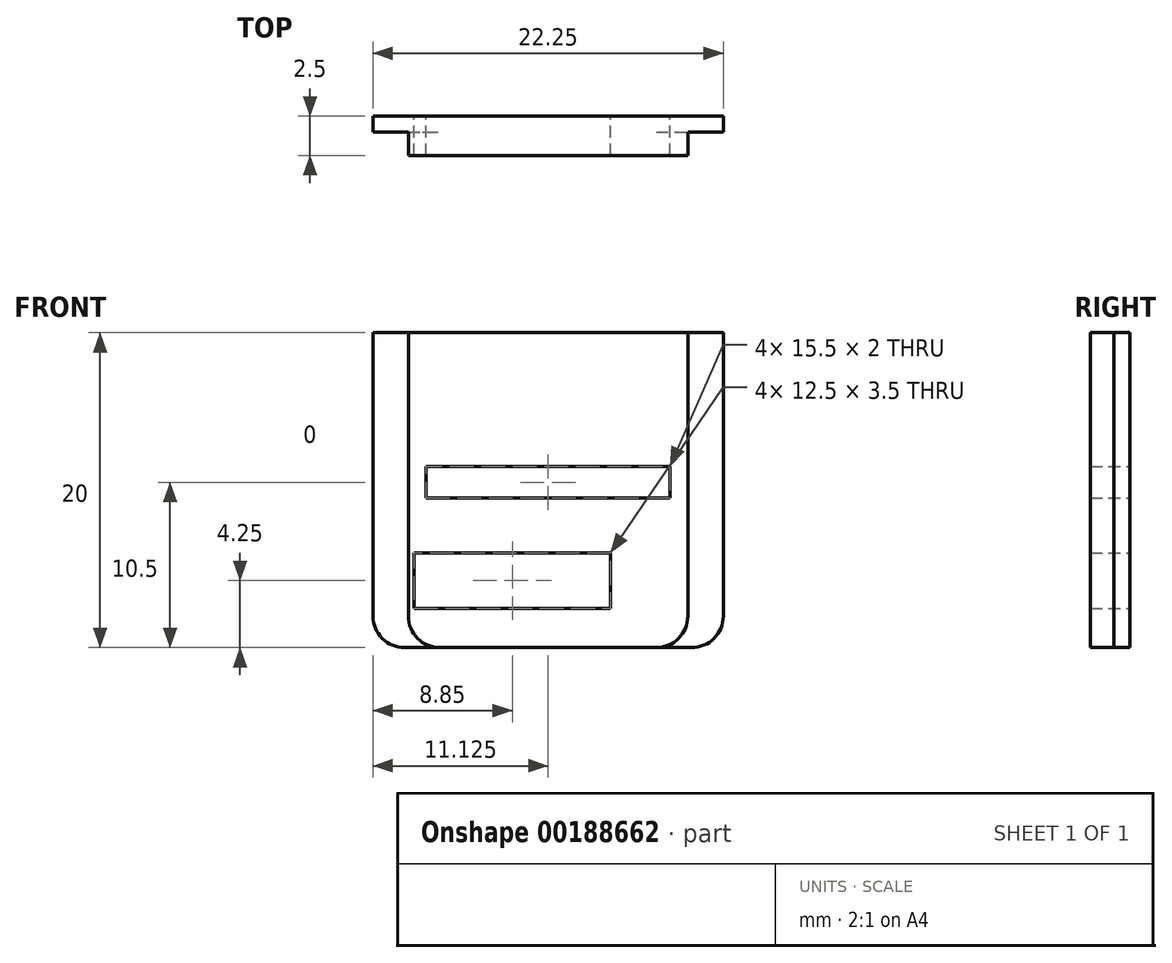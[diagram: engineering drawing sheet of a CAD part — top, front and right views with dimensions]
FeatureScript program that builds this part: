
annotation { "Feature Type Name" : "Feature", "Feature Type Description" : "" }
export const myFeature = defineFeature(function(context is Context, id is Id, definition is map)
    precondition{}
    {
        {
            var Q0;
            Q0=qCreatedBy(makeId("Front.planeOp"),FACE);
            var sketch = newSketch(context, id + "F0", { "sketchPlane" : qUnion([Q0])});
            skLineSegment(sketch, "E0.bottom", {"start": v(2, 0) * mm, "end": v(20.25, 0) * mm});
            skLineSegment(sketch, "E0.top", {"start": v(0, 20) * mm, "end": v(22.25, 20) * mm});
            skLineSegment(sketch, "E0.left", {"start": v(0, 2) * mm, "end": v(0, 20) * mm});
            skLineSegment(sketch, "E0.right", {"start": v(22.25, 2) * mm, "end": v(22.25, 20) * mm});
            skPoint(sketch, "E1.visualSharp", {"position": v(0, 0) * mm});
            skArc(sketch, "E1.filletArc", {"start": v(0, 2) * mm, "mid": v(0.59, 0.59) * mm, "end": v(2, 0) * mm});
            skPoint(sketch, "E2.visualSharp", {"position": v(22.25, 0) * mm});
            skArc(sketch, "E2.filletArc", {"start": v(20.25, 0) * mm, "mid": v(21.66, 0.59) * mm, "end": v(22.25, 2) * mm});
            skSolve(sketch);
        }
        {
            var Q0;
            Q0=qSketchRegion(id+"F0",true);
            extrude(context, id + "F1", {"entities" : qUnion([Q0]), "depth" : 1 * mm});
        }
        {
            var Q0;
            Q0=makeQuery(id+"F1.opExtrude","CAP_FACE",FACE,{"disambiguationData":[OSD([sQuery(id+"F0.wireOp",EDGE,"E0.bottom"),sQuery(id+"F0.wireOp",EDGE,"E0.top"),sQuery(id+"F0.wireOp",EDGE,"E0.left"),sQuery(id+"F0.wireOp",EDGE,"E0.right")])],"isStart":false});
            var sketch = newSketch(context, id + "F2", { "sketchPlane" : qUnion([Q0])});
            skLineSegment(sketch, "E3.bottom", {"start": v(2.25, 20) * mm, "end": v(20, 20) * mm});
            skLineSegment(sketch, "E3.top", {"start": v(4.25, 0) * mm, "end": v(18, 0) * mm});
            skLineSegment(sketch, "E3.left", {"start": v(2.25, 20) * mm, "end": v(2.25, 2) * mm});
            skLineSegment(sketch, "E3.right", {"start": v(20, 20) * mm, "end": v(20, 2) * mm});
            skPoint(sketch, "E4", {"position": v(11.12, 20) * mm});
            skPoint(sketch, "E5.visualSharp", {"position": v(2.25, 0) * mm});
            skArc(sketch, "E5.filletArc", {"start": v(2.25, 2) * mm, "mid": v(2.84, 0.59) * mm, "end": v(4.25, 0) * mm});
            skPoint(sketch, "E6.visualSharp", {"position": v(20, 0) * mm});
            skArc(sketch, "E6.filletArc", {"start": v(18, 0) * mm, "mid": v(19.41, 0.59) * mm, "end": v(20, 2) * mm});
            skSolve(sketch);
        }
        {
            var Q0;
            Q0=qSketchRegion(id+"F2",true);
            extrude(context, id + "F3", {"entities" : qUnion([Q0]), "depth" : 1.5 * mm});
        }
        {
            var Q0;
            Q0=makeQuery(id+"F1.opExtrude","SWEPT_BODY",BODY,{"disambiguationData":[OSD([sQuery(id+"F0.wireOp",EDGE,"E0.bottom"),sQuery(id+"F0.wireOp",EDGE,"E0.top"),sQuery(id+"F0.wireOp",EDGE,"E0.left"),sQuery(id+"F0.wireOp",EDGE,"E0.right")])]});
            var Q1;
            Q1=makeQuery(id+"F3.opExtrude","SWEPT_BODY",BODY,{"disambiguationData":[OSD([sQuery(id+"F2.wireOp",EDGE,"E3.bottom"),sQuery(id+"F2.wireOp",EDGE,"E3.top"),sQuery(id+"F2.wireOp",EDGE,"E3.left"),sQuery(id+"F2.wireOp",EDGE,"E3.right")])]});
            booleanBodies(context, id + "F4", {"operationType" : BooleanOperationType.UNION, "tools" : qUnion([Q0, Q1])});
        }
        {
            var Q0;
            Q0=makeQuery(id+"F1.opExtrude","CAP_FACE",FACE,{"disambiguationData":[OSD([sQuery(id+"F0.wireOp",EDGE,"E0.bottom"),sQuery(id+"F0.wireOp",EDGE,"E0.top"),sQuery(id+"F0.wireOp",EDGE,"E0.left"),sQuery(id+"F0.wireOp",EDGE,"E0.right")])],"isStart":true});
            var sketch = newSketch(context, id + "F5", { "sketchPlane" : qUnion([Q0])});
            skLineSegment(sketch, "E7.bottom", {"start": v(-15.1, 6) * mm, "end": v(-2.6, 6) * mm});
            skLineSegment(sketch, "E7.top", {"start": v(-15.1, 2.5) * mm, "end": v(-2.6, 2.5) * mm});
            skLineSegment(sketch, "E7.left", {"start": v(-15.1, 6) * mm, "end": v(-15.1, 2.5) * mm});
            skLineSegment(sketch, "E7.right", {"start": v(-2.6, 6) * mm, "end": v(-2.6, 2.5) * mm});
            skLineSegment(sketch, "E8.bottom", {"start": v(-18.87, 11.5) * mm, "end": v(-3.37, 11.5) * mm});
            skLineSegment(sketch, "E8.top", {"start": v(-18.87, 9.5) * mm, "end": v(-3.37, 9.5) * mm});
            skLineSegment(sketch, "E8.left", {"start": v(-18.87, 11.5) * mm, "end": v(-18.87, 9.5) * mm});
            skLineSegment(sketch, "E8.right", {"start": v(-3.37, 11.5) * mm, "end": v(-3.37, 9.5) * mm});
            skPoint(sketch, "E9", {"position": v(-11.12, 20) * mm});
            skPoint(sketch, "E10", {"position": v(-11.12, 11.5) * mm});
            skPoint(sketch, "E11", {"position": v(-8.85, 2.5) * mm});
            skSolve(sketch);
        }
        {
            var Q0;
            Q0=qSketchRegion(id+"F5",true);
            extrude(context, id + "F6", {"entities" : qUnion([Q0]), "operationType" : NewBodyOperationType.REMOVE, "endBound" : BoundingType.UP_TO_NEXT, "oppositeDirection" : true, "depth" : 25 * mm});
        }
    });
